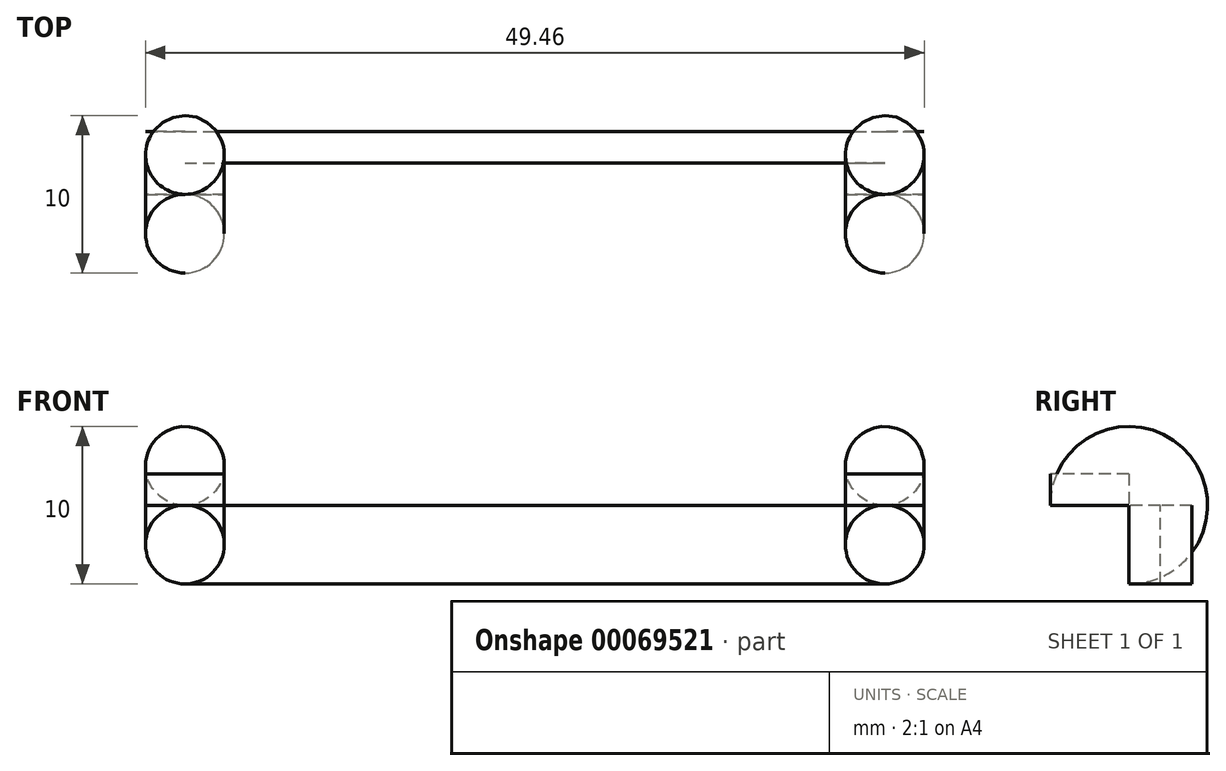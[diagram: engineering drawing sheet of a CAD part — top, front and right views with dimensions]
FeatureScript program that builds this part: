
annotation { "Feature Type Name" : "Feature", "Feature Type Description" : "" }
export const myFeature = defineFeature(function(context is Context, id is Id, definition is map)
    precondition{}
    {
        {
            var Q0;
            Q0=qCreatedBy(makeId("Front.planeOp"),FACE);
            var sketch = newSketch(context, id + "F0", { "sketchPlane" : qUnion([Q0])});
            skLineSegment(sketch, "E0", {"start": v(0, 0) * mm, "end": v(0, 50) * mm, "construction": true});
            skLineSegment(sketch, "E1", {"start": v(0, 0) * mm, "end": v(-22.23, 0) * mm, "construction": true});
            skLineSegment(sketch, "E2.MirrorCS", {"start": v(0, 0) * mm, "end": v(22.23, 0) * mm, "construction": true});
            skCircle(sketch, "E3", {"center": v(-22.23, 0) * mm, "radius": 2.5 * mm});
            skLineSegment(sketch, "E4.bottom", {"start": v(-22.23, -2.5) * mm, "end": v(22.23, -2.5) * mm});
            skLineSegment(sketch, "E4.top", {"start": v(-22.23, 2.5) * mm, "end": v(22.23, 2.5) * mm});
            skLineSegment(sketch, "E4.left", {"start": v(-22.23, -2.5) * mm, "end": v(-22.23, 2.5) * mm});
            skLineSegment(sketch, "E4.right", {"start": v(22.23, -2.5) * mm, "end": v(22.23, 2.5) * mm});
            skPoint(sketch, "E4.middle", {"position": v(0, 0) * mm});
            skCircle(sketch, "E5.MirrorC", {"center": v(22.23, 0) * mm, "radius": 2.5 * mm});
            skSolve(sketch);
        }
        {
            var Q0;
            Q0=qSketchRegion(id+"F0",true);
            var Q1;
            Q1=makeQuery(id+"F0.imprint","IMPRINT",FACE,{"disambiguationData":[TD([[makeQuery(id+"F0.imprint","IMPRINT",EDGE,{"derivedFrom":sQuery(id+"F0.wireOp",EDGE,"E3")}),1.0]])]});
            var Q2;
            Q2=makeQuery(id+"F0.imprint","IMPRINT",FACE,{"disambiguationData":[TD([[makeQuery(id+"F0.imprint","IMPRINT",EDGE,{"derivedFrom":sQuery(id+"F0.wireOp",EDGE,"E5.MirrorC")}),-1.0]])]});
            extrude(context, id + "F1", {"entities" : qUnion([Q0, Q1, Q2]), "oppositeDirection" : true, "depth" : 2 * mm});
        }
        {
            var Q0;
            {var subQ0=sQuery(id+"F0.wireOp",EDGE,"E4.left");Q0=makeQuery(id+"F0.imprint","IMPRINT",FACE,{"disambiguationData":[TD([[makeQuery(id+"F0.imprint","IMPRINT",EDGE,{"derivedFrom":subQ0}),1.0]])]});}
            var Q1;
            {var subQ0=sQuery(id+"F0.wireOp",EDGE,"E4.left");Q1=makeQuery(id+"F0.imprint","IMPRINT",FACE,{"disambiguationData":[TD([[makeQuery(id+"F0.imprint","IMPRINT",EDGE,{"derivedFrom":subQ0}),-1.0]])]});}
            var Q2;
            {var subQ0=sQuery(id+"F0.wireOp",EDGE,"E4.right");Q2=makeQuery(id+"F0.imprint","IMPRINT",FACE,{"disambiguationData":[TD([[makeQuery(id+"F0.imprint","IMPRINT",EDGE,{"derivedFrom":subQ0}),-1.0]])]});}
            var Q3;
            {var subQ0=sQuery(id+"F0.wireOp",EDGE,"E4.right");Q3=makeQuery(id+"F0.imprint","IMPRINT",FACE,{"disambiguationData":[TD([[makeQuery(id+"F0.imprint","IMPRINT",EDGE,{"derivedFrom":subQ0}),1.0]])]});}
            var Q4;
            Q4=sQuery(id+"F0.wireOp",EDGE,"E5.MirrorC");
            var Q5;
            Q5=sQuery(id+"F0.wireOp",EDGE,"E4.left");
            var Q6;
            Q6=sQuery(id+"F0.wireOp",EDGE,"E3");
            extrude(context, id + "F2", {"entities" : qUnion([Q0, Q1, Q2, Q3]), "operationType" : NewBodyOperationType.ADD, "surfaceEntities" : qUnion([Q4, Q5, Q6]), "depth" : 2 * mm});
        }
        {
            var Q0;
            Q0=makeQuery(id+"F2.opExtrude","CAP_FACE",FACE,{"disambiguationData":[OSD([sQuery(id+"F0.wireOp",EDGE,"E3")])],"isStart":false});
            var sketch = newSketch(context, id + "F3", { "sketchPlane" : qUnion([Q0])});
            skLineSegment(sketch, "E6", {"start": v(-22.23, 2.5) * mm, "end": v(22.66, 2.5) * mm, "construction": true});
            skSolve(sketch);
        }
        {
            var Q0;
            Q0=makeQuery(id+"F3.imprint","IMPRINT",FACE,{"disambiguationData":[TD([[makeQuery(id+"F3.imprint","IMPRINT",EDGE,{"derivedFrom":makeQuery(id+"F2.opExtrude","CAP_EDGE",EDGE,{"disambiguationData":[OSD([sQuery(id+"F0.wireOp",EDGE,"E3")])],"isStart":false})}),1.0]])]});
            var Q1;
            Q1=makeQuery(id+"F2.opExtrude","CAP_FACE",FACE,{"disambiguationData":[OSD([sQuery(id+"F0.wireOp",EDGE,"E5.MirrorC")])],"isStart":false});
            var Q2;
            Q2=sQuery(id+"F3.wireOp",EDGE,"E6");
            revolve(context, id + "F4", {"operationType" : NewBodyOperationType.ADD, "entities" : qUnion([Q0, Q1]), "axis" : qUnion([Q2]), "revolveType" : RevolveType.ONE_DIRECTION, "oppositeDirection" : true, "angle" : 90 * degree});
        }
        {
            var Q0;
            Q0=makeQuery(id+"F4.opRevolve","CAP_FACE",FACE,{"disambiguationData":[OSD([sQuery(id+"F0.wireOp",EDGE,"E3")])],"isStart":false});
            var Q1;
            Q1=makeQuery(id+"F4.opRevolve","CAP_FACE",FACE,{"disambiguationData":[OSD([sQuery(id+"F0.wireOp",EDGE,"E5.MirrorC")])],"isStart":false});
            extrude(context, id + "F5", {"entities" : qUnion([Q0, Q1]), "operationType" : NewBodyOperationType.ADD, "depth" : 2 * mm});
        }
    });
